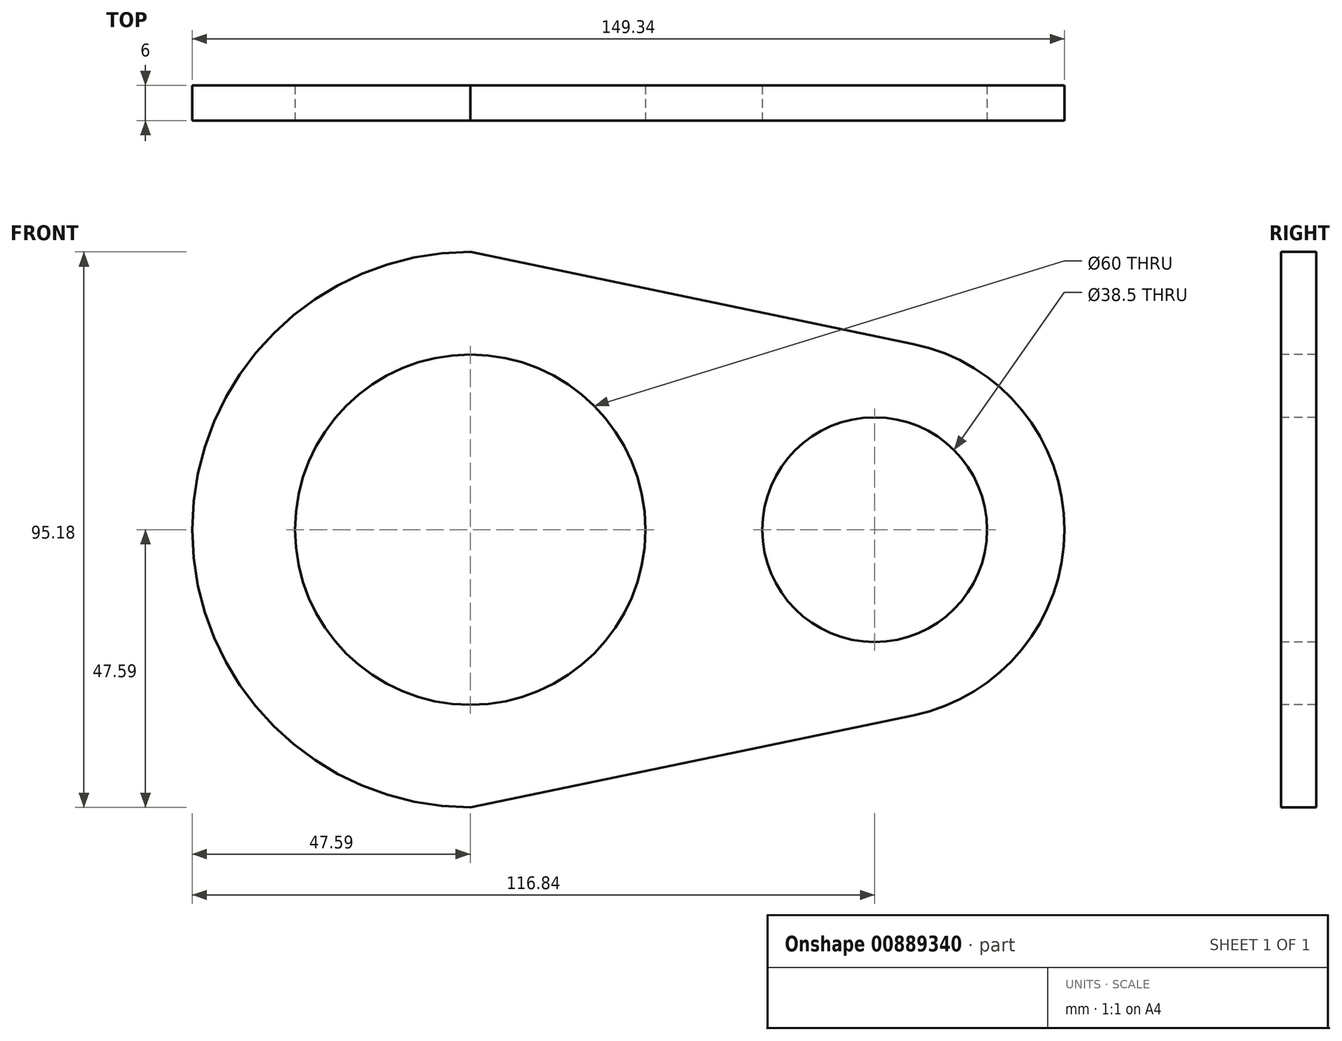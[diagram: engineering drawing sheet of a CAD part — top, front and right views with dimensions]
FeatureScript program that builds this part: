
annotation { "Feature Type Name" : "Feature", "Feature Type Description" : "" }
export const myFeature = defineFeature(function(context is Context, id is Id, definition is map)
    precondition{}
    {
        {
            var Q0;
            Q0=qCreatedBy(makeId("Front.planeOp"),FACE);
            var sketch = newSketch(context, id + "F0", { "sketchPlane" : qUnion([Q0])});
            skCircle(sketch, "E0", {"center": v(-69.25, 0) * mm, "radius": 30 * mm});
            skCircle(sketch, "E1", {"center": v(0, 0) * mm, "radius": 19.25 * mm});
            skArc(sketch, "E2", {"start": v(-69.25, 47.6) * mm, "mid": v(-116.84, 0) * mm, "end": v(-69.25, -47.6) * mm});
            skArc(sketch, "E3", {"start": v(6.61, -31.82) * mm, "mid": v(32.5, 0) * mm, "end": v(6.61, 31.82) * mm});
            skPoint(sketch, "E4.end.orphan", {"position": v(0, -33.55) * mm});
            skPoint(sketch, "E5.end.orphan", {"position": v(0, 32.5) * mm});
            skPoint(sketch, "E6.end.orphan", {"position": v(0, -32.5) * mm});
            skLineSegment(sketch, "E7", {"start": v(6.61, 31.82) * mm, "end": v(-69.25, 47.6) * mm});
            skLineSegment(sketch, "E8", {"start": v(6.61, -31.82) * mm, "end": v(-69.25, -47.6) * mm});
            skSolve(sketch);
        }
        {
            var Q0;
            Q0 = qSketchRegion(id + "F0", true);
            extrude(context, id + "F1", {"entities" : qUnion([Q0]), "oppositeDirection" : true, "depth" : 6 * mm, "offsetDistance" : 25 * mm});
        }
    });
